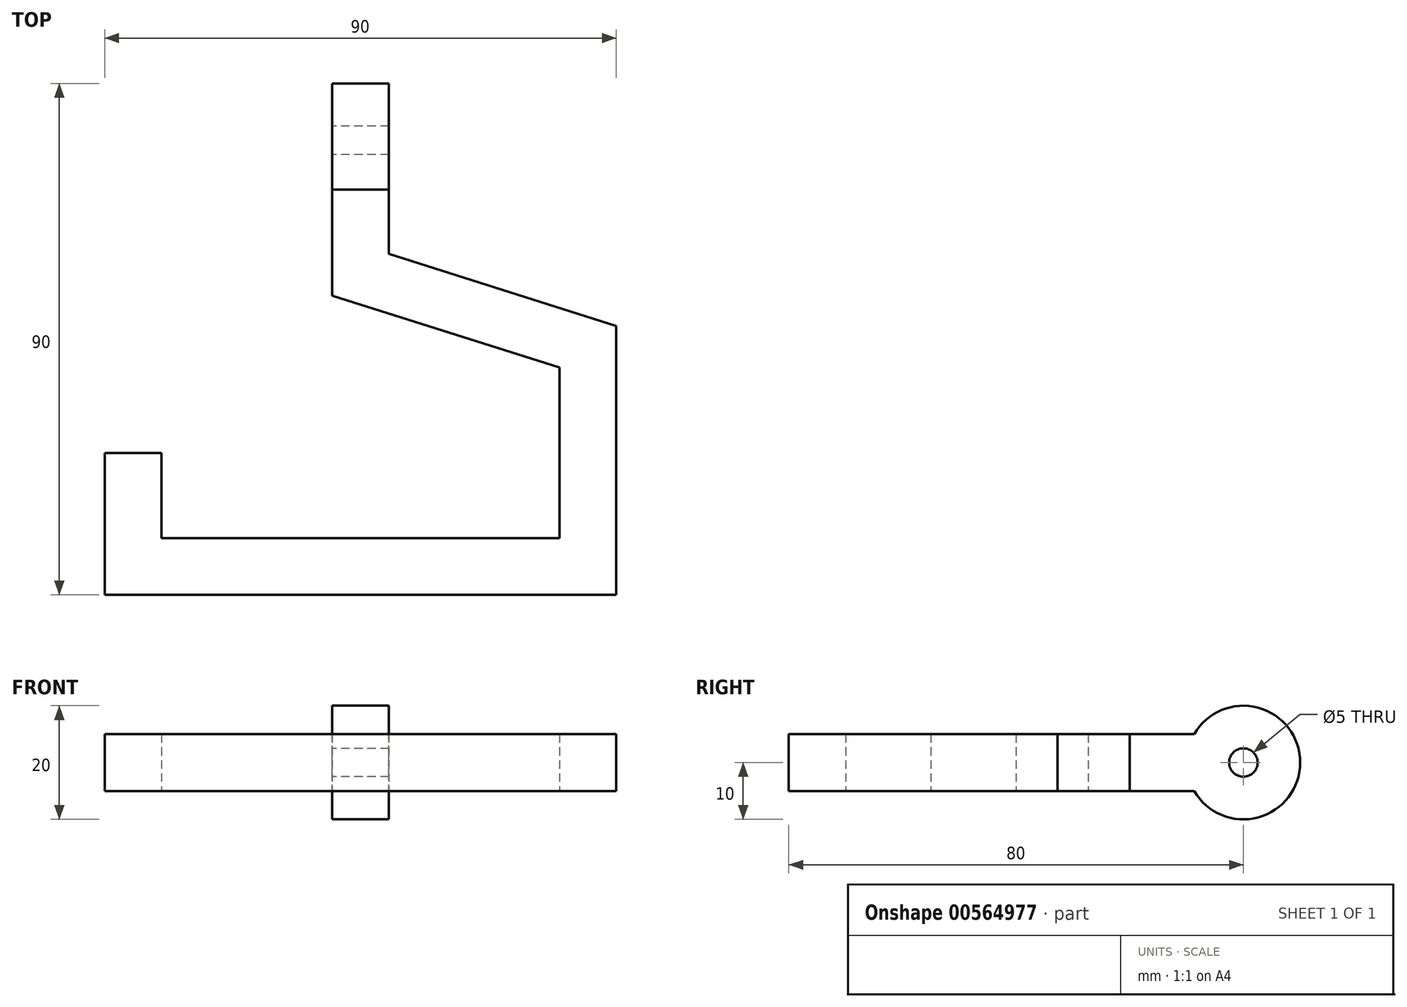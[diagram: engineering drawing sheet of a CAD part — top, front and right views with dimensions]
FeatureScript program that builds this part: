
annotation { "Feature Type Name" : "Feature", "Feature Type Description" : "" }
export const myFeature = defineFeature(function(context is Context, id is Id, definition is map)
    precondition{}
    {
        {
            var Q0;
            Q0=qCreatedBy(makeId("Top.planeOp"),FACE);
            var sketch = newSketch(context, id + "F0", { "sketchPlane" : qUnion([Q0])});
            skPoint(sketch, "E0", {"position": v(0, -40) * mm});
            skLineSegment(sketch, "E1", {"start": v(0, -40) * mm, "end": v(-45, -40) * mm});
            skLineSegment(sketch, "E2", {"start": v(-45, -40) * mm, "end": v(-45, -15) * mm});
            skLineSegment(sketch, "E3", {"start": v(35, -30) * mm, "end": v(35, 0) * mm});
            skLineSegment(sketch, "E4", {"start": v(0, -40) * mm, "end": v(45, -40) * mm});
            skLineSegment(sketch, "E5", {"start": v(45, -40) * mm, "end": v(45, 0) * mm});
            skLineSegment(sketch, "E6", {"start": v(-45, -15) * mm, "end": v(-35, -15) * mm});
            skLineSegment(sketch, "E7", {"start": v(-35, -15) * mm, "end": v(-35, -30) * mm});
            skLineSegment(sketch, "E8", {"start": v(-35, -30) * mm, "end": v(35, -30) * mm});
            skPoint(sketch, "E9", {"position": v(0, 31.34) * mm});
            skLineSegment(sketch, "E10", {"start": v(5, 31.34) * mm, "end": v(5, 20) * mm});
            skLineSegment(sketch, "E11", {"start": v(-5, 31.34) * mm, "end": v(-5, 12.68) * mm});
            skLineSegment(sketch, "E12", {"start": v(-5, 12.68) * mm, "end": v(35, 0) * mm});
            skLineSegment(sketch, "E13", {"start": v(45, 0) * mm, "end": v(45, 7.32) * mm});
            skLineSegment(sketch, "E14", {"start": v(45, 7.32) * mm, "end": v(5, 20) * mm});
            skLineSegment(sketch, "E15", {"start": v(-5, 31.34) * mm, "end": v(5, 31.34) * mm});
            skSolve(sketch);
        }
        {
            var Q0;
            Q0=makeQuery(id+"F0.imprint","IMPRINT",FACE,{"disambiguationData":[TD([[makeQuery(id+"F0.imprint","IMPRINT",EDGE,{"derivedFrom":sQuery(id+"F0.wireOp",EDGE,"E1")}),-1.0]])]});
            extrude(context, id + "F1", {"entities" : qUnion([Q0]), "endBound" : BoundingType.SYMMETRIC, "depth" : 10 * mm, "offsetDistance" : 25 * mm});
        }
        {
            var Q0;
            Q0=qCreatedBy(makeId("Right.planeOp"),FACE);
            var sketch = newSketch(context, id + "F2", { "sketchPlane" : qUnion([Q0])});
            skPoint(sketch, "E16", {"position": v(40, 0) * mm});
            skCircle(sketch, "E17", {"center": v(40, 0) * mm, "radius": 2.5 * mm});
            skPoint(sketch, "E18", {"position": v(31.34, 5) * mm});
            skPoint(sketch, "E19", {"position": v(31.34, -5) * mm});
            skArc(sketch, "E20", {"start": v(31.34, -5) * mm, "mid": v(50, 0) * mm, "end": v(31.34, 5) * mm});
            skLineSegment(sketch, "E21", {"start": v(31.34, 5) * mm, "end": v(31.34, -5) * mm});
            skSolve(sketch);
        }
        {
            var Q0;
            Q0=makeQuery(id+"F2.imprint","IMPRINT",FACE,{"disambiguationData":[TD([[makeQuery(id+"F2.imprint","IMPRINT",EDGE,{"derivedFrom":sQuery(id+"F2.wireOp",EDGE,"E17")}),-1.0]])]});
            extrude(context, id + "F3", {"entities" : qUnion([Q0]), "operationType" : NewBodyOperationType.ADD, "endBound" : BoundingType.SYMMETRIC, "depth" : 10 * mm, "offsetDistance" : 25 * mm});
        }
    });
